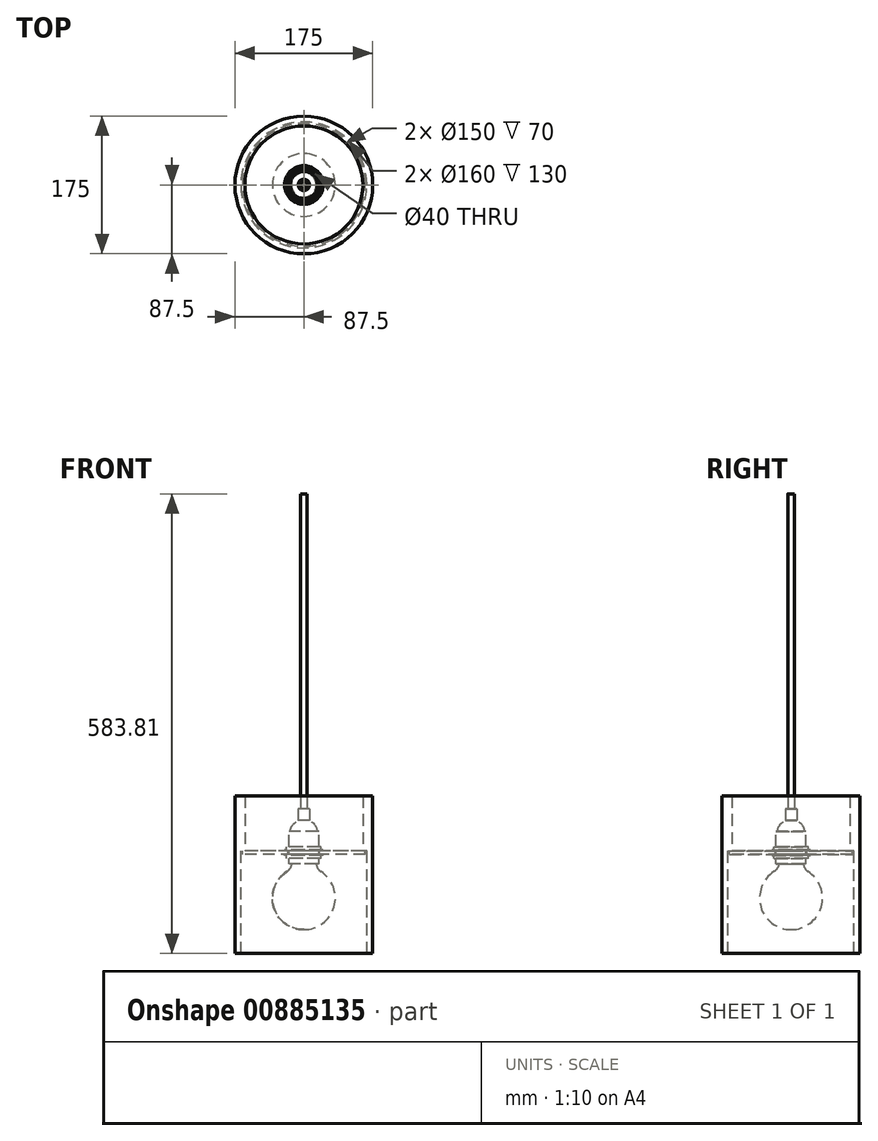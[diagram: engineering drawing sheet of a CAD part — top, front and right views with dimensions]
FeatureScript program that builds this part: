
annotation { "Feature Type Name" : "Feature", "Feature Type Description" : "" }
export const myFeature = defineFeature(function(context is Context, id is Id, definition is map)
    precondition{}
    {
        {
            var Q0;
            Q0=qCreatedBy(makeId("Top.planeOp"),FACE);
            var sketch = newSketch(context, id + "F0", { "sketchPlane" : qUnion([Q0])});
            skCircle(sketch, "E0", {"center": v(0, 0) * mm, "radius": 26 * mm, "construction": true});
            skCircle(sketch, "E1", {"center": v(0, 0) * mm, "radius": 87.5 * mm});
            skSolve(sketch);
        }
        {
            var Q0;
            Q0=qSketchRegion(id+"F0",true);
            extrude(context, id + "F1", {"entities" : qUnion([Q0]), "oppositeDirection" : true, "depth" : 200 * mm, "offsetDistance" : 25 * mm});
        }
        {
            var Q0;
            Q0=qCreatedBy(makeId("Top.planeOp"),FACE);
            cPlane(context, id + "F2", {"entities" : qUnion([Q0]), "cplaneType" : CPlaneType.OFFSET, "offset" : 70 * mm, "oppositeDirection" : true, "width" : 150 * mm, "height" : 150 * mm});
        }
        {
            var Q0;
            Q0=qCreatedBy(id+"F2.planeOp",FACE);
            var sketch = newSketch(context, id + "F3", { "sketchPlane" : qUnion([Q0])});
            skCircle(sketch, "E2.0", {"center": v(0, 0) * mm, "radius": 26 * mm, "construction": true});
            skCircle(sketch, "E3", {"center": v(0, 0) * mm, "radius": 75 * mm});
            skSolve(sketch);
        }
        {
            var Q0;
            Q0=qSketchRegion(id+"F3",true);
            extrude(context, id + "F4", {"entities" : qUnion([Q0]), "operationType" : NewBodyOperationType.REMOVE, "endBound" : BoundingType.THROUGH_ALL, "depth" : 25 * mm, "offsetDistance" : 25 * mm});
        }
        {
            var Q0;
            Q0=qCreatedBy(id+"F2.planeOp",FACE);
            var sketch = newSketch(context, id + "F5", { "sketchPlane" : qUnion([Q0])});
            skCircle(sketch, "E4.0", {"center": v(0, 0) * mm, "radius": 26 * mm, "construction": true});
            skCircle(sketch, "E5", {"center": v(0, 0) * mm, "radius": 80 * mm});
            skSolve(sketch);
        }
        {
            var Q0;
            Q0=qSketchRegion(id+"F5",true);
            extrude(context, id + "F6", {"entities" : qUnion([Q0]), "operationType" : NewBodyOperationType.REMOVE, "endBound" : BoundingType.THROUGH_ALL, "oppositeDirection" : true, "depth" : 25 * mm, "offsetDistance" : 25 * mm});
        }
        {
            var Q0;
            Q0=qCreatedBy(id+"F2.planeOp",FACE);
            var sketch = newSketch(context, id + "F7", { "sketchPlane" : qUnion([Q0])});
            skCircle(sketch, "E6", {"center": v(0, 0) * mm, "radius": 25 * mm});
            skSolve(sketch);
        }
        {
            var Q0;
            Q0=qSketchRegion(id+"F7",true);
            extrude(context, id + "F8", {"entities" : qUnion([Q0]), "oppositeDirection" : true, "depth" : 100 * mm, "offsetDistance" : 25 * mm});
        }
        {
            var Q0;
            Q0=makeQuery(id+"F8.opExtrude","CAP_FACE",FACE,{"disambiguationData":[OSD([sQuery(id+"F7.wireOp",EDGE,"E6")])],"isStart":true});
            var sketch = newSketch(context, id + "F9", { "sketchPlane" : qUnion([Q0])});
            skCircle(sketch, "E7", {"center": v(0, 0) * mm, "radius": 6 * mm});
            skSolve(sketch);
        }
        {
            var Q0;
            Q0=qSketchRegion(id+"F9",true);
            extrude(context, id + "F10", {"entities" : qUnion([Q0]), "operationType" : NewBodyOperationType.ADD, "depth" : 20 * mm, "offsetDistance" : 25 * mm});
        }
        {
            var Q0;
            Q0=makeQuery(id+"F10.opExtrude","CAP_FACE",FACE,{"disambiguationData":[OSD([sQuery(id+"F9.wireOp",EDGE,"E7")])],"isStart":false});
            var sketch = newSketch(context, id + "F11", { "sketchPlane" : qUnion([Q0])});
            skCircle(sketch, "E8", {"center": v(0, 0) * mm, "radius": 3 * mm});
            skSolve(sketch);
        }
        {
            var Q0;
            Q0=qSketchRegion(id+"F11",true);
            extrude(context, id + "F12", {"entities" : qUnion([Q0]), "operationType" : NewBodyOperationType.ADD, "depth" : 200 * mm, "offsetDistance" : 25 * mm});
        }
        {
            var Q0;
            Q0=makeQuery(id+"F8.opExtrude","SWEPT_BODY",BODY,{"disambiguationData":[OSD([sQuery(id+"F7.wireOp",EDGE,"E6")])]});
            deleteBodies(context, id + "F13", {"entities" : qUnion([Q0])});
        }
        {
            var Q0;
            Q0=qCreatedBy(id+"F2.planeOp",FACE);
            var sketch = newSketch(context, id + "F14", { "sketchPlane" : qUnion([Q0])});
            skCircle(sketch, "E9.0", {"center": v(0, 0) * mm, "radius": 26 * mm, "construction": true});
            skCircle(sketch, "E9.1", {"center": v(0, 0) * mm, "radius": 80 * mm, "construction": true});
            skCircle(sketch, "E10", {"center": v(0, 0) * mm, "radius": 78 * mm});
            skCircle(sketch, "E11", {"center": v(0, 0) * mm, "radius": 20 * mm});
            skSolve(sketch);
        }
        {
            var Q0;
            Q0 = qSketchRegion(id + "F14", true);
            extrude(context, id + "F15", {"entities" : qUnion([Q0]), "oppositeDirection" : true, "depth" : 4 * mm, "offsetDistance" : 25 * mm});
        }
        {
            var Q0;
            Q0=qCreatedBy(makeId("Front.planeOp"),FACE);
            var sketch = newSketch(context, id + "F16", { "sketchPlane" : qUnion([Q0])});
            skLineSegment(sketch, "E12", {"start": v(0, 0) * mm, "end": v(0, -86.19) * mm, "construction": true});
            skLineSegment(sketch, "E13", {"start": v(0, -86.19) * mm, "end": v(-19, -86.19) * mm});
            skLineSegment(sketch, "E14", {"start": v(-19, -86.19) * mm, "end": v(-19, -45.13) * mm});
            skLineSegment(sketch, "E15", {"start": v(-5.02, -31.19) * mm, "end": v(0, -31.19) * mm});
            skLineSegment(sketch, "E16", {"start": v(0, -31.19) * mm, "end": v(0, -86.19) * mm});
            skLineSegment(sketch, "E17", {"start": v(-19, -45.13) * mm, "end": v(-17.3, -45.13) * mm});
            skArc(sketch, "E18", {"start": v(-5.02, -31.19) * mm, "mid": v(-13.6, -36.01) * mm, "end": v(-17.3, -45.13) * mm});
            skLineSegment(sketch, "E19.bottom", {"start": v(-19, -69.89) * mm, "end": v(-24.57, -69.89) * mm});
            skLineSegment(sketch, "E19.top", {"start": v(-19, -68.29) * mm, "end": v(-24.57, -68.29) * mm});
            skLineSegment(sketch, "E19.left", {"start": v(-19, -69.89) * mm, "end": v(-19, -68.29) * mm});
            skLineSegment(sketch, "E19.right", {"start": v(-24.57, -69.89) * mm, "end": v(-24.57, -68.29) * mm});
            skLineSegment(sketch, "E20.bottom", {"start": v(-19, -68.29) * mm, "end": v(-21.77, -68.29) * mm});
            skLineSegment(sketch, "E20.top", {"start": v(-19, -64.62) * mm, "end": v(-21.77, -64.62) * mm});
            skLineSegment(sketch, "E20.left", {"start": v(-19, -68.29) * mm, "end": v(-19, -64.62) * mm});
            skLineSegment(sketch, "E20.right", {"start": v(-21.77, -68.29) * mm, "end": v(-21.77, -64.62) * mm});
            skLineSegment(sketch, "E21.bottom", {"start": v(-19, -74.11) * mm, "end": v(-24.57, -74.11) * mm});
            skLineSegment(sketch, "E21.top", {"start": v(-19, -75.64) * mm, "end": v(-24.57, -75.64) * mm});
            skLineSegment(sketch, "E21.left", {"start": v(-19, -74.11) * mm, "end": v(-19, -75.64) * mm});
            skLineSegment(sketch, "E21.right", {"start": v(-24.57, -74.11) * mm, "end": v(-24.57, -75.64) * mm});
            skLineSegment(sketch, "E22.bottom", {"start": v(-19, -75.64) * mm, "end": v(-21.77, -75.64) * mm});
            skLineSegment(sketch, "E22.top", {"start": v(-19, -79.32) * mm, "end": v(-21.77, -79.32) * mm});
            skLineSegment(sketch, "E22.left", {"start": v(-19, -75.64) * mm, "end": v(-19, -79.32) * mm});
            skLineSegment(sketch, "E22.right", {"start": v(-21.77, -75.64) * mm, "end": v(-21.77, -79.32) * mm});
            skSolve(sketch);
        }
        {
            var Q0;
            Q0 = qSketchRegion(id + "F16", true);
            var Q1;
            Q1=sQuery(id+"F16.wireOp",EDGE,"E12");
            revolve(context, id + "F17", {"surfaceOperationType" : NewSurfaceOperationType.NEW, "entities" : qUnion([Q0]), "axis" : qUnion([Q1]), "revolveType" : RevolveType.FULL});
        }
        {
            var Q0;
            Q0=qCreatedBy(makeId("Front.planeOp"),FACE);
            var sketch = newSketch(context, id + "F18", { "sketchPlane" : qUnion([Q0])});
            skArc(sketch, "E23", {"start": v(0, -89.7) * mm, "mid": v(-40, -129.7) * mm, "end": v(0, -169.7) * mm});
            skLineSegment(sketch, "E24", {"start": v(0, -89.7) * mm, "end": v(0, -169.7) * mm});
            skLineSegment(sketch, "E25", {"start": v(0, -89.7) * mm, "end": v(0, -86.17) * mm});
            skLineSegment(sketch, "E26", {"start": v(0, -86.17) * mm, "end": v(-15.75, -86.17) * mm});
            skArc(sketch, "E27", {"start": v(-21.57, -96.01) * mm, "mid": v(-17.48, -91.78) * mm, "end": v(-15.75, -86.17) * mm});
            skSolve(sketch);
        }
        {
            var Q0;
            Q0 = qSketchRegion(id + "F18", true);
            var Q1;
            Q1=sQuery(id+"F18.wireOp",EDGE,"E24");
            revolve(context, id + "F19", {"surfaceOperationType" : NewSurfaceOperationType.NEW, "entities" : qUnion([Q0]), "axis" : qUnion([Q1]), "revolveType" : RevolveType.FULL});
        }
        {
            var Q0;
            Q0=makeQuery(id+"F17.opRevolve","SWEPT_FACE",FACE,{"disambiguationData":[OSD([sQuery(id+"F16.wireOp",EDGE,"E15")])]});
            var sketch = newSketch(context, id + "F20", { "sketchPlane" : qUnion([Q0])});
            skCircle(sketch, "E28", {"center": v(0, 0) * mm, "radius": 7.2 * mm});
            skSolve(sketch);
        }
        {
            var Q0;
            Q0 = qSketchRegion(id + "F20", true);
            extrude(context, id + "F21", {"entities" : qUnion([Q0]), "operationType" : NewBodyOperationType.ADD, "depth" : 15 * mm, "offsetDistance" : 25 * mm});
        }
        {
            var Q0;
            Q0=makeQuery(id+"F21.opExtrude","CAP_FACE",FACE,{"disambiguationData":[OSD([sQuery(id+"F20.wireOp",EDGE,"E28")])],"isStart":false});
            var sketch = newSketch(context, id + "F22", { "sketchPlane" : qUnion([Q0])});
            skCircle(sketch, "E29", {"center": v(0, 0) * mm, "radius": 4 * mm});
            skSolve(sketch);
        }
        {
            var Q0;
            Q0 = qSketchRegion(id + "F22", true);
            extrude(context, id + "F23", {"entities" : qUnion([Q0]), "depth" : 400 * mm, "offsetDistance" : 25 * mm});
        }
    });
